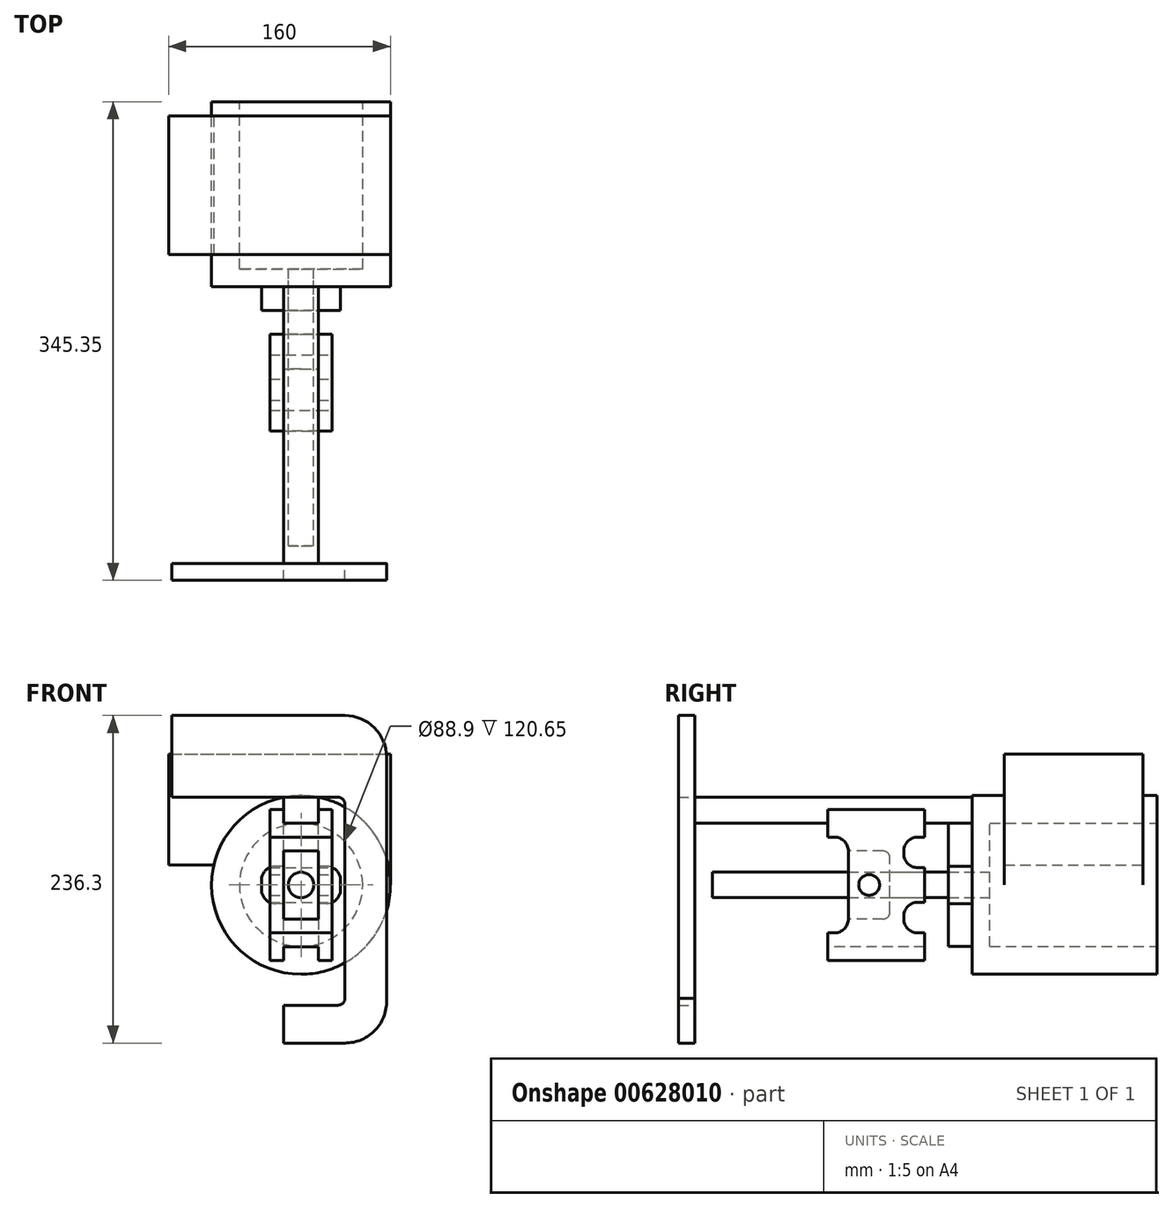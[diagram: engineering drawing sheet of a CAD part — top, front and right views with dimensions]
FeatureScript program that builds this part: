
annotation { "Feature Type Name" : "Feature", "Feature Type Description" : "" }
export const myFeature = defineFeature(function(context is Context, id is Id, definition is map)
    precondition{}
    {
        {
            var Q0;
            Q0=qCreatedBy(makeId("Front.planeOp"),FACE);
            var sketch = newSketch(context, id + "F0", { "sketchPlane" : qUnion([Q0])});
            skCircle(sketch, "E0", {"center": v(0, 0) * mm, "radius": 44.45 * mm});
            skArc(sketch, "E1", {"start": v(-62.8, 14.45) * mm, "mid": v(-7.27, -64.04) * mm, "end": v(64.45, 0) * mm});
            skLineSegment(sketch, "E2.right", {"start": v(-95.55, 94.45) * mm, "end": v(-95.55, 14.45) * mm});
            skLineSegment(sketch, "E3", {"start": v(-95.55, 14.45) * mm, "end": v(-62.8, 14.45) * mm});
            skLineSegment(sketch, "E4", {"start": v(64.45, 0) * mm, "end": v(64.45, 94.45) * mm});
            skLineSegment(sketch, "E5", {"start": v(-95.55, 94.45) * mm, "end": v(64.45, 94.45) * mm});
            skCircle(sketch, "E6", {"center": v(0, 0) * mm, "radius": 64.45 * mm});
            skSolve(sketch);
        }
        {
            var Q0;
            Q0=makeQuery(id+"F0.imprint","IMPRINT",FACE,{"disambiguationData":[TD([[makeQuery(id+"F0.imprint","IMPRINT",EDGE,{"derivedFrom":sQuery(id+"F0.wireOp",EDGE,"E2.right")}),1.0]])]});
            extrude(context, id + "F1", {"entities" : qUnion([Q0]), "endBound" : BoundingType.SYMMETRIC, "depth" : 100 * mm, "offsetDistance" : 25 * mm});
        }
        {
            var Q0;
            Q0=makeQuery(id+"F0.imprint","IMPRINT",FACE,{"disambiguationData":[TD([[makeQuery(id+"F0.imprint","IMPRINT",EDGE,{"derivedFrom":sQuery(id+"F0.wireOp",EDGE,"E0")}),-1.0]])]});
            extrude(context, id + "F2", {"entities" : qUnion([Q0]), "operationType" : NewBodyOperationType.ADD, "endBound" : BoundingType.SYMMETRIC, "depth" : 120.65 * mm, "offsetDistance" : 25 * mm});
        }
        {
            var Q0;
            Q0=makeQuery(id+"F2.opExtrude","CAP_FACE",FACE,{"disambiguationData":[OSD([sQuery(id+"F0.wireOp",EDGE,"E0"),sQuery(id+"F0.wireOp",EDGE,"E6")])],"isStart":false});
            var sketch = newSketch(context, id + "F3", { "sketchPlane" : qUnion([Q0])});
            skCircle(sketch, "E7", {"center": v(0, 0) * mm, "radius": 9.2 * mm});
            skLineSegment(sketch, "E8.bottom", {"start": v(-12.5, 44.45) * mm, "end": v(12.5, 44.45) * mm});
            skLineSegment(sketch, "E8.top", {"start": v(-12.5, -44.45) * mm, "end": v(12.5, -44.45) * mm});
            skLineSegment(sketch, "E9.top", {"start": v(-18.55, -13.42) * mm, "end": v(-12.5, -13.42) * mm});
            skLineSegment(sketch, "E9.left", {"start": v(-28.55, 3.43) * mm, "end": v(-28.55, -3.42) * mm});
            skLineSegment(sketch, "E9.right", {"start": v(28.55, 3.43) * mm, "end": v(28.55, -3.42) * mm});
            skPoint(sketch, "E10.visualSharp", {"position": v(-28.55, 13.42) * mm});
            skArc(sketch, "E10.filletArc", {"start": v(-18.55, 13.43) * mm, "mid": v(-25.62, 10.5) * mm, "end": v(-28.55, 3.43) * mm});
            skPoint(sketch, "E11.visualSharp", {"position": v(-28.55, -13.42) * mm});
            skArc(sketch, "E11.filletArc", {"start": v(-28.55, -3.42) * mm, "mid": v(-25.62, -10.5) * mm, "end": v(-18.55, -13.42) * mm});
            skPoint(sketch, "E12.visualSharp", {"position": v(28.55, -13.42) * mm});
            skArc(sketch, "E12.filletArc", {"start": v(18.55, -13.42) * mm, "mid": v(25.62, -10.5) * mm, "end": v(28.55, -3.42) * mm});
            skPoint(sketch, "E13.visualSharp", {"position": v(28.55, 13.42) * mm});
            skArc(sketch, "E13.filletArc", {"start": v(28.55, 3.43) * mm, "mid": v(25.62, 10.5) * mm, "end": v(18.55, 13.43) * mm});
            skLineSegment(sketch, "E14", {"start": v(12.5, -13.42) * mm, "end": v(18.55, -13.42) * mm});
            skLineSegment(sketch, "E15.trimOffspring", {"start": v(12.5, 13.43) * mm, "end": v(18.55, 13.43) * mm});
            skLineSegment(sketch, "E16", {"start": v(-18.55, 13.43) * mm, "end": v(-12.5, 13.43) * mm});
            skLineSegment(sketch, "E17", {"start": v(12.5, 44.45) * mm, "end": v(12.5, 13.43) * mm});
            skLineSegment(sketch, "E18", {"start": v(-12.5, 44.45) * mm, "end": v(-12.5, 13.43) * mm});
            skLineSegment(sketch, "E19", {"start": v(-12.5, -13.42) * mm, "end": v(-12.5, -44.45) * mm});
            skLineSegment(sketch, "E20", {"start": v(12.5, -44.45) * mm, "end": v(12.5, -13.42) * mm});
            skCircle(sketch, "E21", {"center": v(0, 0) * mm, "radius": 44.45 * mm});
            skSolve(sketch);
        }
        {
            var Q0;
            Q0 = qSketchRegion(id + "F3", true);
            var Q1;
            {var subQ1=sQuery(id+"F3.wireOp",EDGE,"E9.top");Q1=makeQuery(id+"F3.imprint","IMPRINT",FACE,{"disambiguationData":[TD([[makeQuery(id+"F3.imprint","IMPRINT",EDGE,{"derivedFrom":subQ1}),-1.0]])]});}
            var Q2;
            Q2=makeQuery(id+"F3.imprint","IMPRINT",FACE,{"disambiguationData":[TD([[makeQuery(id+"F3.imprint","IMPRINT",EDGE,{"derivedFrom":sQuery(id+"F3.wireOp",EDGE,"E9.right")}),1.0]])]});
            var Q3;
            Q3=makeQuery(id+"F3.imprint","IMPRINT",FACE,{"disambiguationData":[TD([[makeQuery(id+"F3.imprint","IMPRINT",EDGE,{"derivedFrom":makeQuery(id+"F2.opExtrude","CAP_EDGE",EDGE,{"disambiguationData":[OSD([sQuery(id+"F0.wireOp",EDGE,"E6")])],"isStart":false})}),1.0]])]});
            extrude(context, id + "F4", {"entities" : qUnion([Q0, Q1, Q2, Q3]), "depth" : 12.7 * mm, "offsetDistance" : 25 * mm});
        }
        {
            var Q0;
            Q0=makeQuery(id+"F3.imprint","IMPRINT",FACE,{"disambiguationData":[TD([[makeQuery(id+"F3.imprint","IMPRINT",EDGE,{"derivedFrom":sQuery(id+"F3.wireOp",EDGE,"E7")}),-1.0]])]});
            var Q1;
            {var subQ0=sQuery(id+"F3.wireOp",EDGE,"E19");var subQ1=sQuery(id+"F3.wireOp",EDGE,"E8.top");var subQ2=makeQuery(id+"F3.imprint","INTERSECT",VERTEX,{"derivedFrom":[subQ1,subQ0]});Q1=makeQuery(id+"F3.imprint","IMPRINT",FACE,{"disambiguationData":[TD([[makeQuery(id+"F3.imprint","IMPRINT",EDGE,{"disambiguationData":[TD([[subQ2,-1.0]])],"derivedFrom":subQ1}),1.0]])]});}
            var Q2;
            {var subQ0=sQuery(id+"F3.wireOp",EDGE,"E20");var subQ1=sQuery(id+"F3.wireOp",EDGE,"E8.top");var subQ2=makeQuery(id+"F3.imprint","INTERSECT",VERTEX,{"derivedFrom":[subQ1,subQ0]});Q2=makeQuery(id+"F3.imprint","IMPRINT",FACE,{"disambiguationData":[TD([[makeQuery(id+"F3.imprint","IMPRINT",EDGE,{"disambiguationData":[TD([[subQ2,1.0]])],"derivedFrom":subQ1}),1.0]])]});}
            var Q3;
            {var subQ0=sQuery(id+"F3.wireOp",EDGE,"E17");var subQ1=sQuery(id+"F3.wireOp",EDGE,"E8.bottom");var subQ2=makeQuery(id+"F3.imprint","INTERSECT",VERTEX,{"derivedFrom":[subQ1,subQ0]});Q3=makeQuery(id+"F3.imprint","IMPRINT",FACE,{"disambiguationData":[TD([[makeQuery(id+"F3.imprint","IMPRINT",EDGE,{"disambiguationData":[TD([[subQ2,1.0]])],"derivedFrom":subQ1}),-1.0]])]});}
            var Q4;
            {var subQ0=sQuery(id+"F3.wireOp",EDGE,"E18");var subQ1=sQuery(id+"F3.wireOp",EDGE,"E8.bottom");var subQ2=makeQuery(id+"F3.imprint","INTERSECT",VERTEX,{"derivedFrom":[subQ1,subQ0]});Q4=makeQuery(id+"F3.imprint","IMPRINT",FACE,{"disambiguationData":[TD([[makeQuery(id+"F3.imprint","IMPRINT",EDGE,{"disambiguationData":[TD([[subQ2,-1.0]])],"derivedFrom":subQ1}),-1.0]])]});}
            extrude(context, id + "F5", {"entities" : qUnion([Q0, Q1, Q2, Q3, Q4]), "operationType" : NewBodyOperationType.ADD, "depth" : 30 * mm, "offsetDistance" : 25 * mm});
        }
        {
            var Q0;
            Q0=makeQuery(id+"F4.opExtrude","CAP_FACE",FACE,{"disambiguationData":[OSD([sQuery(id+"F0.wireOp",EDGE,"E6"),sQuery(id+"F3.wireOp",EDGE,"E7")])],"isStart":false});
            var sketch = newSketch(context, id + "F6", { "sketchPlane" : qUnion([Q0])});
            skLineSegment(sketch, "E22", {"start": v(-12.5, 44.45) * mm, "end": v(0, 44.45) * mm});
            skLineSegment(sketch, "E23", {"start": v(-12.5, 63.23) * mm, "end": v(0, 63.23) * mm});
            skLineSegment(sketch, "E24", {"start": v(-12.5, 44.45) * mm, "end": v(-12.5, 63.23) * mm});
            skLineSegment(sketch, "E25", {"start": v(12.5, 44.45) * mm, "end": v(12.5, 63.23) * mm});
            skLineSegment(sketch, "E26", {"start": v(0, 44.45) * mm, "end": v(0, 63.23) * mm, "construction": true});
            skLineSegment(sketch, "E27", {"start": v(0, 63.23) * mm, "end": v(12.5, 63.23) * mm});
            skLineSegment(sketch, "E28", {"start": v(0, 44.45) * mm, "end": v(12.5, 44.45) * mm});
            skSolve(sketch);
        }
        {
            var Q0;
            Q0=makeQuery(id+"F6.imprint","IMPRINT",FACE,{"disambiguationData":[TD([[makeQuery(id+"F6.imprint","IMPRINT",EDGE,{"derivedFrom":sQuery(id+"F6.wireOp",EDGE,"E22")}),-1.0]])]});
            extrude(context, id + "F7", {"entities" : qUnion([Q0]), "depth" : 200 * mm, "offsetDistance" : 25 * mm});
        }
        {
            var Q0;
            Q0=makeQuery(id+"F7.opExtrude","SWEPT_FACE",FACE,{"disambiguationData":[OSD([sQuery(id+"F6.wireOp",EDGE,"E24")])]});
            var sketch = newSketch(context, id + "F8", { "sketchPlane" : qUnion([Q0])});
            skLineSegment(sketch, "E29.top", {"start": v(107.43, 44.45) * mm, "end": v(177.43, 44.45) * mm});
            skLineSegment(sketch, "E30", {"start": v(177.43, 44.45) * mm, "end": v(107.43, 44.45) * mm});
            skLineSegment(sketch, "E31", {"start": v(107.43, -44.57) * mm, "end": v(177.43, -44.57) * mm});
            skLineSegment(sketch, "E32", {"start": v(107.43, 44.45) * mm, "end": v(107.43, 34.45) * mm});
            skLineSegment(sketch, "E33", {"start": v(177.43, 44.45) * mm, "end": v(177.43, 34.45) * mm});
            skLineSegment(sketch, "E34", {"start": v(177.43, -44.57) * mm, "end": v(177.43, -54.57) * mm});
            skLineSegment(sketch, "E35", {"start": v(177.43, -54.57) * mm, "end": v(107.43, -54.57) * mm});
            skLineSegment(sketch, "E36", {"start": v(107.43, -54.57) * mm, "end": v(107.43, -44.57) * mm});
            skLineSegment(sketch, "E37", {"start": v(122.43, -0.06) * mm, "end": v(162.43, -0.06) * mm, "construction": true});
            skCircle(sketch, "E38", {"center": v(147.43, 0) * mm, "radius": 7.5 * mm});
            skLineSegment(sketch, "E39", {"start": v(107.43, 44.45) * mm, "end": v(107.43, 54.45) * mm});
            skLineSegment(sketch, "E40", {"start": v(107.43, 54.45) * mm, "end": v(177.43, 54.45) * mm});
            skLineSegment(sketch, "E41", {"start": v(177.43, 54.45) * mm, "end": v(177.43, 44.45) * mm});
            skLineSegment(sketch, "E42", {"start": v(107.43, -34.57) * mm, "end": v(107.43, -34.57) * mm});
            skLineSegment(sketch, "E43", {"start": v(107.43, 34.45) * mm, "end": v(112.43, 34.45) * mm});
            skLineSegment(sketch, "E44", {"start": v(107.43, -34.57) * mm, "end": v(107.43, -44.57) * mm});
            skLineSegment(sketch, "E45", {"start": v(107.43, -34.57) * mm, "end": v(112.43, -34.57) * mm});
            skLineSegment(sketch, "E46", {"start": v(122.43, -24.57) * mm, "end": v(122.43, -24.57) * mm});
            skLineSegment(sketch, "E47", {"start": v(162.43, 24.45) * mm, "end": v(162.43, -24.57) * mm});
            skLineSegment(sketch, "E48.trimOffspring", {"start": v(177.43, -34.57) * mm, "end": v(177.43, -44.57) * mm});
            skLineSegment(sketch, "E49", {"start": v(172.43, 34.45) * mm, "end": v(177.43, 34.45) * mm});
            skLineSegment(sketch, "E50", {"start": v(172.43, -34.57) * mm, "end": v(177.43, -34.57) * mm});
            skArc(sketch, "E51.filletArc", {"start": v(122.43, 24.45) * mm, "mid": v(119.5, 31.52) * mm, "end": v(112.43, 34.45) * mm});
            skPoint(sketch, "E52.visualSharp", {"position": v(162.43, 34.45) * mm});
            skArc(sketch, "E52.filletArc", {"start": v(172.43, 34.45) * mm, "mid": v(165.35, 31.52) * mm, "end": v(162.43, 24.45) * mm});
            skArc(sketch, "E53.filletArc", {"start": v(112.43, -34.57) * mm, "mid": v(119.5, -31.64) * mm, "end": v(122.43, -24.57) * mm});
            skArc(sketch, "E54.filletArc", {"start": v(162.43, -24.57) * mm, "mid": v(165.35, -31.64) * mm, "end": v(172.43, -34.57) * mm});
            skLineSegment(sketch, "E55", {"start": v(127.43, -0.06) * mm, "end": v(122.43, -0.06) * mm});
            skLineSegment(sketch, "E56", {"start": v(107.43, -0.06) * mm, "end": v(107.43, 12.44) * mm});
            skLineSegment(sketch, "E57", {"start": v(107.43, 12.44) * mm, "end": v(107.43, -0.06) * mm});
            skLineSegment(sketch, "E58", {"start": v(107.43, -0.06) * mm, "end": v(107.43, -12.56) * mm});
            skLineSegment(sketch, "E59", {"start": v(112.43, -12.56) * mm, "end": v(107.43, -12.56) * mm});
            skLineSegment(sketch, "E60", {"start": v(107.43, 12.44) * mm, "end": v(112.43, 12.44) * mm});
            skLineSegment(sketch, "E61", {"start": v(122.43, 22.44) * mm, "end": v(122.43, 24.45) * mm});
            skLineSegment(sketch, "E62", {"start": v(127.43, -0.06) * mm, "end": v(107.43, -0.06) * mm, "construction": true});
            skLineSegment(sketch, "E63", {"start": v(122.43, -24.57) * mm, "end": v(122.43, -22.56) * mm});
            skArc(sketch, "E64.filletArc", {"start": v(122.43, -22.56) * mm, "mid": v(119.5, -15.49) * mm, "end": v(112.43, -12.56) * mm});
            skArc(sketch, "E65.filletArc", {"start": v(112.43, 12.44) * mm, "mid": v(119.5, 15.37) * mm, "end": v(122.43, 22.44) * mm});
            skSolve(sketch);
        }
        {
            var Q0;
            Q0 = qSketchRegion(id + "F8", true);
            extrude(context, id + "F9", {"entities" : qUnion([Q0]), "depth" : 10 * mm, "offsetDistance" : 25 * mm});
        }
        {
            var Q0;
            Q0 = qSketchRegion(id + "F8", true);
            extrude(context, id + "F10", {"entities" : qUnion([Q0]), "operationType" : NewBodyOperationType.ADD, "oppositeDirection" : true, "depth" : 35 * mm, "offsetDistance" : 25 * mm});
        }
        {
            var Q0;
            Q0=makeQuery(id+"F8.imprint","IMPRINT",FACE,{"disambiguationData":[TD([[makeQuery(id+"F8.imprint","IMPRINT",EDGE,{"derivedFrom":sQuery(id+"F8.wireOp",EDGE,"E30")}),-1.0]])]});
            var Q1;
            Q1=makeQuery(id+"F8.imprint","IMPRINT",FACE,{"disambiguationData":[TD([[makeQuery(id+"F8.imprint","IMPRINT",EDGE,{"derivedFrom":sQuery(id+"F8.wireOp",EDGE,"E31")}),-1.0]])]});
            extrude(context, id + "F11", {"entities" : qUnion([Q0, Q1]), "operationType" : NewBodyOperationType.REMOVE, "oppositeDirection" : true, "depth" : 25 * mm, "offsetDistance" : 25 * mm});
        }
        {
            var Q0;
            {var subQ0=sQuery(id+"F8.wireOp",EDGE,"E47");Q0=makeQuery(id+"F10.boolean.opBoolean","MERGE",FACE,{"derivedFrom":[makeQuery(id+"F9.opExtrude","SWEPT_FACE",FACE,{"disambiguationData":[OSD([subQ0])]}),makeQuery(id+"F10.opExtrude","SWEPT_FACE",FACE,{"disambiguationData":[OSD([subQ0])]})]});}
            var sketch = newSketch(context, id + "F12", { "sketchPlane" : qUnion([Q0])});
            skLineSegment(sketch, "E66", {"start": v(0, 24.45) * mm, "end": v(0, -24.57) * mm, "construction": true});
            skLineSegment(sketch, "E67", {"start": v(0, -24.57) * mm, "end": v(12.5, -24.57) * mm});
            skLineSegment(sketch, "E68", {"start": v(12.5, -24.57) * mm, "end": v(12.5, 24.45) * mm});
            skLineSegment(sketch, "E69", {"start": v(-12.5, -24.57) * mm, "end": v(-12.5, 24.45) * mm});
            skLineSegment(sketch, "E70", {"start": v(-12.5, -24.57) * mm, "end": v(0, -24.57) * mm});
            skSolve(sketch);
        }
        {
            var Q0;
            Q0=makeQuery(id+"F12.imprint","IMPRINT",FACE,{"disambiguationData":[TD([[makeQuery(id+"F12.imprint","IMPRINT",EDGE,{"derivedFrom":sQuery(id+"F12.wireOp",EDGE,"E67")}),1.0]])]});
            var Q1;
            Q1 = qConstructionFilter(qBodyType(qCreatedBy(id + "F12" ,EDGE), BodyType.WIRE), ConstructionObject.NO);
            extrude(context, id + "F13", {"entities" : qUnion([Q0]), "operationType" : NewBodyOperationType.REMOVE, "surfaceEntities" : qUnion([Q1]), "oppositeDirection" : true, "depth" : 30 * mm, "offsetDistance" : 25 * mm});
        }
        {
            var Q0;
            Q0=makeQuery(id+"F13.boolean.opBoolean","COPY",EDGE,{"derivedFrom":makeQuery(id+"F13.opExtrude","CAP_EDGE",EDGE,{"disambiguationData":[OSD([sQuery(id+"F12.wireOp",EDGE,"E67"),sQuery(id+"F12.wireOp",EDGE,"E70")])],"isStart":false})});
            var Q1;
            Q1=makeQuery(id+"F13.boolean.opBoolean","COPY",EDGE,{"derivedFrom":makeQuery(id+"F13.opExtrude","CAP_EDGE",EDGE,{"disambiguationData":[OSD([sQuery(id+"F8.wireOp",EDGE,"E47"),sQuery(id+"F8.wireOp",EDGE,"E52.filletArc")])],"isStart":false})});
            fillet(context, id + "F14", {"entities" : qUnion([Q0, Q1]), "radius" : 5 * mm, "tangentPropagation" : true, "allowEdgeOverflow" : false});
        }
        {
            var Q0;
            Q0=makeQuery(id+"F3.imprint","IMPRINT",FACE,{"disambiguationData":[TD([[makeQuery(id+"F3.imprint","IMPRINT",EDGE,{"derivedFrom":sQuery(id+"F3.wireOp",EDGE,"E7")}),1.0]])]});
            extrude(context, id + "F15", {"entities" : qUnion([Q0]), "operationType" : NewBodyOperationType.REMOVE, "endBound" : BoundingType.THROUGH_ALL, "depth" : 25 * mm, "offsetDistance" : 25 * mm});
        }
        {
            var Q0;
            Q0=makeQuery(id+"F3.imprint","IMPRINT",FACE,{"disambiguationData":[TD([[makeQuery(id+"F3.imprint","IMPRINT",EDGE,{"derivedFrom":sQuery(id+"F3.wireOp",EDGE,"E7")}),1.0]])]});
            extrude(context, id + "F16", {"entities" : qUnion([Q0]), "depth" : 200 * mm, "offsetDistance" : 25 * mm});
        }
        {
            var Q0;
            Q0=makeQuery(id+"F7.opExtrude","CAP_FACE",FACE,{"disambiguationData":[OSD([sQuery(id+"F6.wireOp",EDGE,"E22"),sQuery(id+"F6.wireOp",EDGE,"E23"),sQuery(id+"F6.wireOp",EDGE,"E24"),sQuery(id+"F6.wireOp",EDGE,"E25"),sQuery(id+"F6.wireOp",EDGE,"E27"),sQuery(id+"F6.wireOp",EDGE,"E28")])],"isStart":false});
            var sketch = newSketch(context, id + "F17", { "sketchPlane" : qUnion([Q0])});
            skLineSegment(sketch, "E71.bottom", {"start": v(12.5, 63.23) * mm, "end": v(26.68, 63.23) * mm});
            skLineSegment(sketch, "E71.top", {"start": v(12.5, -86.77) * mm, "end": v(26.68, -86.77) * mm});
            skLineSegment(sketch, "E71.right", {"start": v(31.68, 58.23) * mm, "end": v(31.68, -81.77) * mm});
            skPoint(sketch, "E72.visualSharp", {"position": v(31.68, 63.23) * mm});
            skArc(sketch, "E72.filletArc", {"start": v(31.68, 58.23) * mm, "mid": v(30.22, 61.76) * mm, "end": v(26.68, 63.23) * mm});
            skPoint(sketch, "E73.visualSharp", {"position": v(31.68, -86.77) * mm});
            skArc(sketch, "E73.filletArc", {"start": v(26.68, -86.77) * mm, "mid": v(30.22, -85.3) * mm, "end": v(31.68, -81.77) * mm});
            skLineSegment(sketch, "E74.bottom", {"start": v(-12.5, 63.23) * mm, "end": v(-12.5, 63.23) * mm});
            skLineSegment(sketch, "E75", {"start": v(61.68, 58.23) * mm, "end": v(61.68, -81.77) * mm});
            skLineSegment(sketch, "E76", {"start": v(61.68, 58.23) * mm, "end": v(61.68, 92.22) * mm});
            skLineSegment(sketch, "E77", {"start": v(31.68, 122.22) * mm, "end": v(-93.32, 122.22) * mm});
            skPoint(sketch, "E78.visualSharp", {"position": v(61.68, 122.22) * mm});
            skArc(sketch, "E78.filletArc", {"start": v(61.68, 92.22) * mm, "mid": v(52.9, 113.43) * mm, "end": v(31.68, 122.22) * mm});
            skLineSegment(sketch, "E79", {"start": v(-93.32, 122.22) * mm, "end": v(-93.32, 63.23) * mm});
            skLineSegment(sketch, "E80", {"start": v(-93.32, 63.23) * mm, "end": v(-12.5, 63.23) * mm});
            skLineSegment(sketch, "E81", {"start": v(12.5, -86.77) * mm, "end": v(-12.5, -86.77) * mm});
            skLineSegment(sketch, "E82", {"start": v(-12.5, -86.77) * mm, "end": v(-12.5, -114.08) * mm});
            skLineSegment(sketch, "E83", {"start": v(-12.5, -114.08) * mm, "end": v(31.77, -114.08) * mm});
            skPoint(sketch, "E84.visualSharp", {"position": v(61.68, -114.08) * mm});
            skArc(sketch, "E84.filletArc", {"start": v(31.77, -114.08) * mm, "mid": v(53.79, -104.46) * mm, "end": v(61.68, -81.77) * mm});
            skSolve(sketch);
        }
        {
            var Q0;
            Q0=makeQuery(id+"F17.imprint","IMPRINT",FACE,{"disambiguationData":[TD([[makeQuery(id+"F17.imprint","IMPRINT",EDGE,{"derivedFrom":sQuery(id+"F17.wireOp",EDGE,"E71.bottom")}),1.0]])]});
            extrude(context, id + "F18", {"entities" : qUnion([Q0]), "depth" : 12 * mm, "offsetDistance" : 25 * mm});
        }
    });
